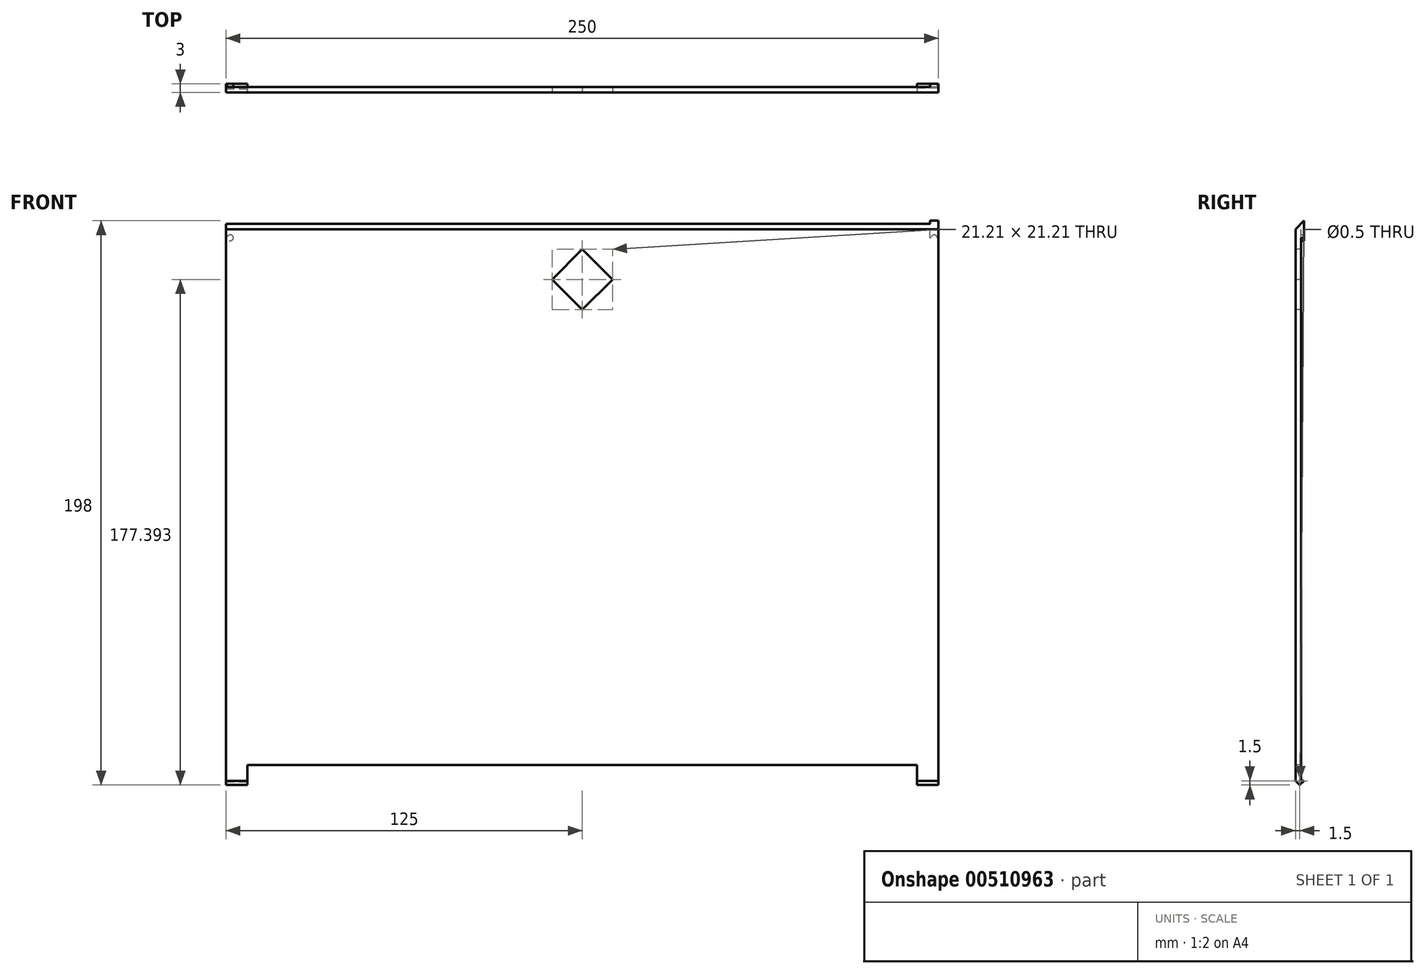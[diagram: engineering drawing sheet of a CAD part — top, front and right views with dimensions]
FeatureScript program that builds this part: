
annotation { "Feature Type Name" : "Feature", "Feature Type Description" : "" }
export const myFeature = defineFeature(function(context is Context, id is Id, definition is map)
    precondition{}
    {
        {
            var Q0;
            Q0=qCreatedBy(makeId("Front.planeOp"),FACE);
            var sketch = newSketch(context, id + "F0", { "sketchPlane" : qUnion([Q0])});
            skLineSegment(sketch, "E0.bottom", {"start": v(-125, -99.25) * mm, "end": v(125, -99.25) * mm});
            skLineSegment(sketch, "E0.top", {"start": v(-125, 99.25) * mm, "end": v(125, 99.25) * mm});
            skLineSegment(sketch, "E0.left", {"start": v(-125, -99.25) * mm, "end": v(-125, 99.25) * mm});
            skLineSegment(sketch, "E0.right", {"start": v(125, -99.25) * mm, "end": v(125, 99.25) * mm});
            skPoint(sketch, "E0.middle", {"position": v(0, 0) * mm});
            skSolve(sketch);
        }
        {
            var Q0;
            Q0=makeQuery(id+"F0.imprint","IMPRINT",FACE,{"disambiguationData":[TD([[makeQuery(id+"F0.imprint","IMPRINT",EDGE,{"derivedFrom":sQuery(id+"F0.wireOp",EDGE,"E0.bottom")}),1.0]])]});
            extrude(context, id + "F1", {"entities" : qUnion([Q0]), "depth" : 3 * mm, "offsetDistance" : 25 * mm});
        }
        {
            var Q0;
            Q0=makeQuery(id+"F1.opExtrude","CAP_FACE",FACE,{"disambiguationData":[OSD([sQuery(id+"F0.wireOp",EDGE,"E0.bottom"),sQuery(id+"F0.wireOp",EDGE,"E0.top"),sQuery(id+"F0.wireOp",EDGE,"E0.left"),sQuery(id+"F0.wireOp",EDGE,"E0.right")])],"isStart":false});
            var sketch = newSketch(context, id + "F2", { "sketchPlane" : qUnion([Q0])});
            skLineSegment(sketch, "E1.bottom", {"start": v(-125, -99.25) * mm, "end": v(-117.5, -99.25) * mm});
            skLineSegment(sketch, "E1.top", {"start": v(-125, -91.75) * mm, "end": v(-117.5, -91.75) * mm});
            skLineSegment(sketch, "E1.left", {"start": v(-125, -99.25) * mm, "end": v(-125, -91.75) * mm});
            skLineSegment(sketch, "E1.right", {"start": v(-117.5, -99.25) * mm, "end": v(-117.5, -91.75) * mm});
            skLineSegment(sketch, "E2.MirrorCS", {"start": v(117.5, -99.25) * mm, "end": v(117.5, -91.75) * mm});
            skLineSegment(sketch, "E3.MirrorCS", {"start": v(125, -99.25) * mm, "end": v(125, -91.75) * mm});
            skLineSegment(sketch, "E4.MirrorCS", {"start": v(125, -91.75) * mm, "end": v(117.5, -91.75) * mm});
            skLineSegment(sketch, "E5.MirrorCS", {"start": v(125, -99.25) * mm, "end": v(117.5, -99.25) * mm});
            skLineSegment(sketch, "E6", {"start": v(117.5, -91.75) * mm, "end": v(-117.5, -91.75) * mm});
            skSolve(sketch);
        }
        {
            var Q0;
            {var subQ0=sQuery(id+"F2.wireOp",EDGE,"E1.right");Q0=makeQuery(id+"F2.imprint","IMPRINT",FACE,{"disambiguationData":[TD([[makeQuery(id+"F2.imprint","IMPRINT",EDGE,{"derivedFrom":subQ0}),-1.0]])]});}
            extrude(context, id + "F3", {"entities" : qUnion([Q0]), "operationType" : NewBodyOperationType.REMOVE, "oppositeDirection" : true, "depth" : 30 * mm, "offsetDistance" : 25 * mm});
        }
        {
            var Q0;
            Q0=makeQuery(id+"F3.boolean.opBoolean","COPY",FACE,{"derivedFrom":makeQuery(id+"F3.opExtrude","SWEPT_FACE",FACE,{"disambiguationData":[OSD([sQuery(id+"F2.wireOp",EDGE,"E1.right")])]})});
            var sketch = newSketch(context, id + "F4", { "sketchPlane" : qUnion([Q0])});
            skLineSegment(sketch, "E7", {"start": v(-1.5, -99.25) * mm, "end": v(-1.5, -97.25) * mm});
            skCircle(sketch, "E8", {"center": v(-1.5, -97.25) * mm, "radius": 0.25 * mm});
            skSolve(sketch);
        }
        {
            var Q0;
            Q0=makeQuery(id+"F4.imprint","IMPRINT",FACE,{"disambiguationData":[TD([[makeQuery(id+"F4.imprint","IMPRINT",EDGE,{"derivedFrom":sQuery(id+"F4.wireOp",EDGE,"E8")}),1.0]])]});
            extrude(context, id + "F5", {"entities" : qUnion([Q0]), "operationType" : NewBodyOperationType.REMOVE, "oppositeDirection" : true, "depth" : 300 * mm, "offsetDistance" : 25 * mm});
        }
        {
            var Q0;
            {var subQ0=sQuery(id+"F0.wireOp",EDGE,"E0.bottom");var subQ1=sQuery(id+"F0.wireOp",EDGE,"E0.left");Q0=makeQuery(id+"F3.boolean.opBoolean","SPLIT",EDGE,{"disambiguationData":[TD([makeQuery(id+"F1.opExtrude","SWEPT_FACE",FACE,{"disambiguationData":[OSD([subQ1])]})])],"derivedFrom":makeQuery(id+"F1.opExtrude","CAP_EDGE",EDGE,{"disambiguationData":[OSD([subQ0])],"isStart":false})});}
            var Q1;
            {var subQ0=sQuery(id+"F0.wireOp",EDGE,"E0.bottom");var subQ1=sQuery(id+"F0.wireOp",EDGE,"E0.left");Q1=makeQuery(id+"F3.boolean.opBoolean","SPLIT",EDGE,{"disambiguationData":[TD([makeQuery(id+"F1.opExtrude","SWEPT_FACE",FACE,{"disambiguationData":[OSD([subQ1])]})])],"derivedFrom":makeQuery(id+"F1.opExtrude","CAP_EDGE",EDGE,{"disambiguationData":[OSD([subQ0])],"isStart":true})});}
            var Q2;
            {var subQ0=sQuery(id+"F0.wireOp",EDGE,"E0.bottom");var subQ1=sQuery(id+"F0.wireOp",EDGE,"E0.right");Q2=makeQuery(id+"F3.boolean.opBoolean","SPLIT",EDGE,{"disambiguationData":[TD([makeQuery(id+"F1.opExtrude","SWEPT_FACE",FACE,{"disambiguationData":[OSD([subQ1])]})])],"derivedFrom":makeQuery(id+"F1.opExtrude","CAP_EDGE",EDGE,{"disambiguationData":[OSD([subQ0])],"isStart":false})});}
            var Q3;
            {var subQ0=sQuery(id+"F0.wireOp",EDGE,"E0.bottom");var subQ1=sQuery(id+"F0.wireOp",EDGE,"E0.right");Q3=makeQuery(id+"F3.boolean.opBoolean","SPLIT",EDGE,{"disambiguationData":[TD([makeQuery(id+"F1.opExtrude","SWEPT_FACE",FACE,{"disambiguationData":[OSD([subQ1])]})])],"derivedFrom":makeQuery(id+"F1.opExtrude","CAP_EDGE",EDGE,{"disambiguationData":[OSD([subQ0])],"isStart":true})});}
            chamfer(context, id + "F6", {"entities" : qUnion([Q0, Q1, Q2, Q3]), "width" : 2 * mm, "tangentPropagation" : true});
        }
        {
            var Q0;
            Q0=makeQuery(id+"F1.opExtrude","CAP_FACE",FACE,{"disambiguationData":[OSD([sQuery(id+"F0.wireOp",EDGE,"E0.bottom"),sQuery(id+"F0.wireOp",EDGE,"E0.top"),sQuery(id+"F0.wireOp",EDGE,"E0.left"),sQuery(id+"F0.wireOp",EDGE,"E0.right")])],"isStart":false});
            var sketch = newSketch(context, id + "F7", { "sketchPlane" : qUnion([Q0])});
            skLineSegment(sketch, "E9.bottom", {"start": v(-10.6, 78.64) * mm, "end": v(0, 89.25) * mm});
            skLineSegment(sketch, "E9.top", {"start": v(0, 68.04) * mm, "end": v(10.6, 78.64) * mm});
            skLineSegment(sketch, "E9.left", {"start": v(-10.6, 78.64) * mm, "end": v(0, 68.04) * mm});
            skLineSegment(sketch, "E9.right", {"start": v(0, 89.25) * mm, "end": v(10.6, 78.64) * mm});
            skPoint(sketch, "E9.middle", {"position": v(0, 32.89) * mm});
            skLineSegment(sketch, "E10", {"start": v(0, 99.25) * mm, "end": v(0, 89.25) * mm});
            skSolve(sketch);
        }
        {
            var Q0;
            Q0=makeQuery(id+"F7.imprint","IMPRINT",FACE,{"disambiguationData":[TD([[makeQuery(id+"F7.imprint","IMPRINT",EDGE,{"derivedFrom":sQuery(id+"F7.wireOp",EDGE,"E9.bottom")}),-1.0]])]});
            extrude(context, id + "F8", {"entities" : qUnion([Q0]), "operationType" : NewBodyOperationType.REMOVE, "oppositeDirection" : true, "depth" : 25 * mm, "offsetDistance" : 25 * mm});
        }
        {
            var Q0;
            Q0=makeQuery(id+"F1.opExtrude","CAP_EDGE",EDGE,{"disambiguationData":[OSD([sQuery(id+"F0.wireOp",EDGE,"E0.top")])],"isStart":false});
            chamfer(context, id + "F9", {"entities" : qUnion([Q0]), "width" : 3 * mm, "tangentPropagation" : true});
        }
        {
            var Q0;
            Q0=makeQuery(id+"F1.opExtrude","CAP_FACE",FACE,{"disambiguationData":[OSD([sQuery(id+"F0.wireOp",EDGE,"E0.bottom"),sQuery(id+"F0.wireOp",EDGE,"E0.top"),sQuery(id+"F0.wireOp",EDGE,"E0.left"),sQuery(id+"F0.wireOp",EDGE,"E0.right")])],"isStart":true});
            var sketch = newSketch(context, id + "F10", { "sketchPlane" : qUnion([Q0])});
            skPoint(sketch, "E11.middle", {"position": v(0, 95.1) * mm});
            skPoint(sketch, "E11.middle.positionSnap0", {"position": v(0, 99.25) * mm});
            skPoint(sketch, "E11.centerSnap0", {"position": v(0, 99.25) * mm});
            skLineSegment(sketch, "E12", {"start": v(-125, 93.25) * mm, "end": v(-122, 93.25) * mm});
            skLineSegment(sketch, "E13", {"start": v(-122, 93.25) * mm, "end": v(-122, 99.25) * mm});
            skLineSegment(sketch, "E14", {"start": v(-123.5, 93.25) * mm, "end": v(-123.5, 99.25) * mm});
            skCircle(sketch, "E15", {"center": v(-123.5, 93.25) * mm, "radius": 1.05 * mm});
            skCircle(sketch, "E16.MirrorC", {"center": v(123.5, 93.25) * mm, "radius": 1.05 * mm});
            skSolve(sketch);
        }
        {
            var Q0;
            {var subQ0=sQuery(id+"F10.wireOp",EDGE,"E12");var subQ1=makeQuery(id+"F10.imprint","INTERSECT",VERTEX,{"derivedFrom":[subQ0,sQuery(id+"F10.wireOp",EDGE,"E14")]});Q0=makeQuery(id+"F10.imprint","IMPRINT",FACE,{"disambiguationData":[TD([[makeQuery(id+"F10.imprint","IMPRINT",EDGE,{"disambiguationData":[TD([[subQ1,1.0]])],"derivedFrom":subQ0}),-1.0]])]});}
            var Q1;
            {var subQ0=sQuery(id+"F10.wireOp",EDGE,"E14");var subQ1=sQuery(id+"F10.wireOp",EDGE,"E12");var subQ2=makeQuery(id+"F10.imprint","INTERSECT",VERTEX,{"derivedFrom":[subQ1,subQ0]});Q1=makeQuery(id+"F10.imprint","IMPRINT",FACE,{"disambiguationData":[TD([[makeQuery(id+"F10.imprint","IMPRINT",EDGE,{"disambiguationData":[TD([[subQ2,-1.0]])],"derivedFrom":subQ1}),1.0]])]});}
            var Q2;
            {var subQ0=sQuery(id+"F10.wireOp",EDGE,"E14");var subQ1=sQuery(id+"F10.wireOp",EDGE,"E12");var subQ2=makeQuery(id+"F10.imprint","INTERSECT",VERTEX,{"derivedFrom":[subQ1,subQ0]});Q2=makeQuery(id+"F10.imprint","IMPRINT",FACE,{"disambiguationData":[TD([[makeQuery(id+"F10.imprint","IMPRINT",EDGE,{"disambiguationData":[TD([[subQ2,1.0]])],"derivedFrom":subQ1}),1.0]])]});}
            var Q3;
            Q3=makeQuery(id+"F10.imprint","IMPRINT",FACE,{"disambiguationData":[TD([[makeQuery(id+"F10.imprint","IMPRINT",EDGE,{"derivedFrom":sQuery(id+"F10.wireOp",EDGE,"E16.MirrorC")}),-1.0]])]});
            extrude(context, id + "F11", {"entities" : qUnion([Q0, Q1, Q2, Q3]), "operationType" : NewBodyOperationType.REMOVE, "oppositeDirection" : true, "depth" : 1.1 * mm, "offsetDistance" : 25 * mm});
        }
    });
